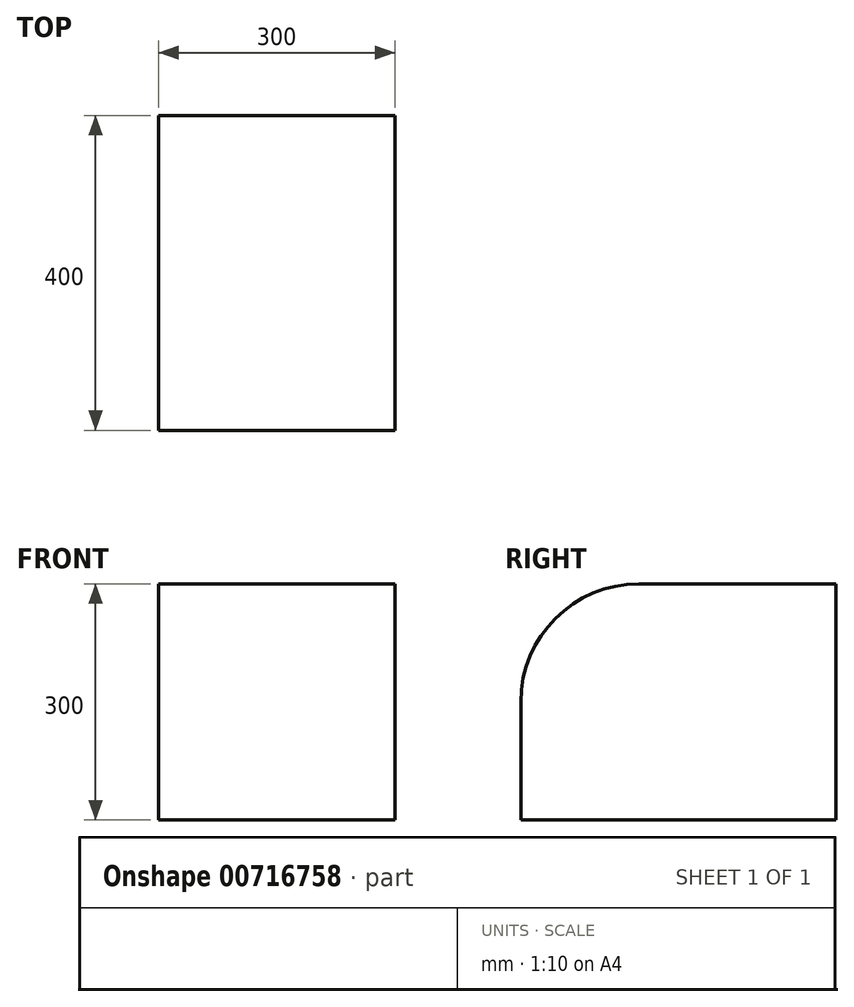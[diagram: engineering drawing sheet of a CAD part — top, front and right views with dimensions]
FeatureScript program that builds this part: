
annotation { "Feature Type Name" : "Feature", "Feature Type Description" : "" }
export const myFeature = defineFeature(function(context is Context, id is Id, definition is map)
    precondition{}
    {
        {
            var Q0;
            Q0=qCreatedBy(makeId("Top.planeOp"),FACE);
            var sketch = newSketch(context, id + "F0", { "sketchPlane" : qUnion([Q0])});
            skLineSegment(sketch, "E0.bottom", {"start": v(150, -200) * mm, "end": v(-150, -200) * mm});
            skLineSegment(sketch, "E0.top", {"start": v(150, 200) * mm, "end": v(-150, 200) * mm});
            skLineSegment(sketch, "E0.left", {"start": v(150, -200) * mm, "end": v(150, 200) * mm});
            skLineSegment(sketch, "E0.right", {"start": v(-150, -200) * mm, "end": v(-150, 200) * mm});
            skPoint(sketch, "E0.middle", {"position": v(0, 0) * mm});
            skSolve(sketch);
        }
        {
            var Q0;
            Q0=makeQuery(id+"F0.imprint","IMPRINT",FACE,{"disambiguationData":[TD([[makeQuery(id+"F0.imprint","IMPRINT",EDGE,{"derivedFrom":sQuery(id+"F0.wireOp",EDGE,"E0.bottom")}),-1.0]])]});
            extrude(context, id + "F1", {"entities" : qUnion([Q0]), "depth" : 300 * mm, "offsetDistance" : 25 * mm});
        }
        {
            var Q0;
            Q0=makeQuery(id+"F1.opExtrude","CAP_EDGE",EDGE,{"disambiguationData":[OSD([sQuery(id+"F0.wireOp",EDGE,"E0.bottom")])],"isStart":false});
            fillet(context, id + "F2", {"entities" : qUnion([Q0]), "radius" : 150 * mm, "tangentPropagation" : true, "allowEdgeOverflow" : false});
        }
    });
